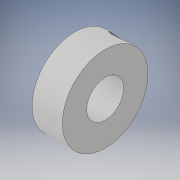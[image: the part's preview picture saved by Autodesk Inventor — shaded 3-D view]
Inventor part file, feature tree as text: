
AUTODESK INVENTOR PART (.ipt)
format: ipt  version: 2019 (Build 230136000, 136)  size: 121,856 bytes
history: native  units: in
note: dims shown in document units (in); Inventor stores cm internally (conversion verified against a paired STEP export)
features: sketch x3, extrude x2, plane x1, thread x1
ambient origin geometry x8: Origin, YZ Plane, XZ Plane, XY Plane, X Axis, Y Axis, Z Axis, Center Point
bodies: Solid1 (feature_tree)
feature tree (7):
  extrude  "Extrusion1"  Depth=0.1575in
  sketch  "Sketch2"  dims[d2=0.1969in d3=0.0in d4=45.0deg d5=0.1969in]
  plane  "Work Plane1"
  extrude  "Extrusion2"  TaperAngle=45.0deg  [1 undecoded]
  thread  "Thread1"  [1 undecoded]
  sketch  "Sketch1"  dims[d0=0.2402in d1=0.1575in]
  sketch  "Sketch3"  dims[d6=180.0deg d7=0.1181in d8=0.1969in d9=0.0in d10=0.3937in d11=0.0in]
note: 2 required parameter values undecoded (feature->parameter linkage not recoverable at this tier; creation-order binding heuristic only, values carry confidence <= 0.55)
